# Revit family: 36_O43101001_Orinal Gotta Entrada Posterior
name_source: partatom
category: Aparatos sanitarios
revit_build: Autodesk Revit 2018 (Build: 20170223_1515(x64)
units: mm (PartAtom-declared; Revit-internal decimal feet)

## family parameters
Anfitrión = Muro
Compartido = No
Corte con vacíos al cargar = No
Cota de conector redondo = Diámetro de uso
Número OmniClass = 23.45.05.21.11.21
Punto de cálculo de habitación = No
Siempre vertical = Sí
Tipo de pieza = Normal
Título OmniClass = Urinals

## types (1)
- Tipo 1
    Consumo de Agua = 0.5 litros por descarga
    Cumple ADA = SI
    Cumple EDGE = SI
    Cumple LEED = SI
    Diametro conexión = 3/4 Pulgada
    Garantía = Garantía CORONA limitada de por vida en elementos de porcelana y 5 años en grifería tanque y asiento
    Marca = CORONA
    Material = Cerámica
    Nombre = Orinal Gotta Entrada Posterior
    Presión Máxima = 125 PSI
    Presión Mínima = 15 PSI
    Referencia = O43101001
    Tipo = Orinal
    URL = https://www.corona.co
    WATER SENSE = SI
